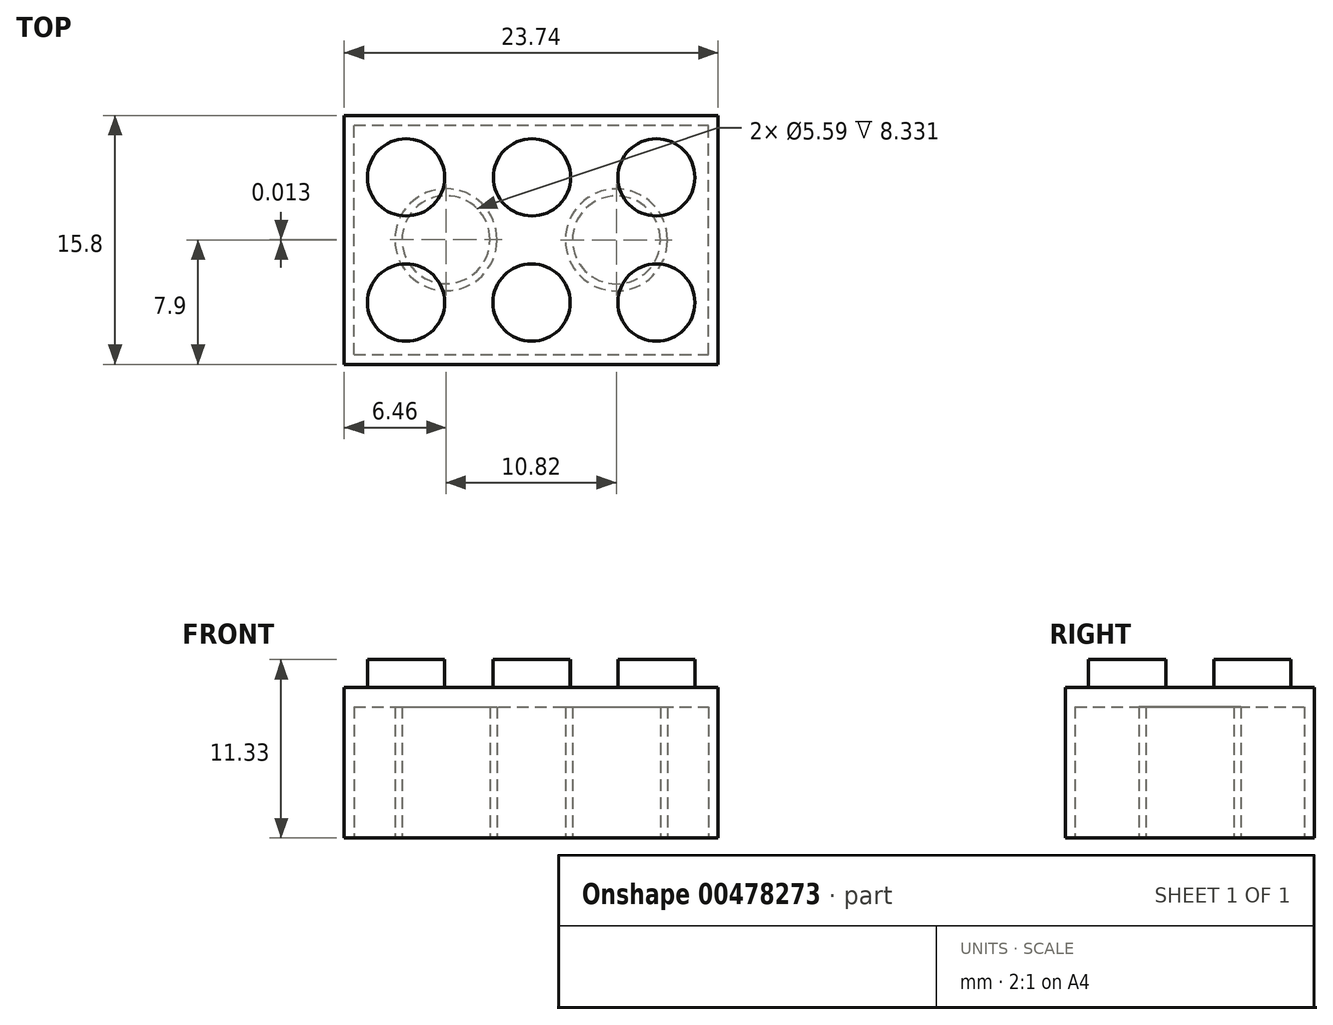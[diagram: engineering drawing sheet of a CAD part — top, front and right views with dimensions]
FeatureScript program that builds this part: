
annotation { "Feature Type Name" : "Feature", "Feature Type Description" : "" }
export const myFeature = defineFeature(function(context is Context, id is Id, definition is map)
    precondition{}
    {
        {
            var Q0;
            Q0=qCreatedBy(makeId("Top.planeOp"),FACE);
            var sketch = newSketch(context, id + "F0", { "sketchPlane" : qUnion([Q0])});
            skLineSegment(sketch, "E0.bottom", {"start": v(-11.87, 7.9) * mm, "end": v(11.87, 7.9) * mm});
            skLineSegment(sketch, "E0.top", {"start": v(-11.87, -7.9) * mm, "end": v(11.87, -7.9) * mm});
            skLineSegment(sketch, "E0.left", {"start": v(-11.87, 7.9) * mm, "end": v(-11.87, -7.9) * mm});
            skLineSegment(sketch, "E0.right", {"start": v(11.87, 7.9) * mm, "end": v(11.87, -7.9) * mm});
            skPoint(sketch, "E0.middle", {"position": v(0, 0) * mm});
            skSolve(sketch);
        }
        {
            var Q0;
            Q0=makeQuery(id+"F0.imprint","IMPRINT",FACE,{"disambiguationData":[TD([[makeQuery(id+"F0.imprint","IMPRINT",EDGE,{"derivedFrom":sQuery(id+"F0.wireOp",EDGE,"E0.bottom")}),-1.0]])]});
            extrude(context, id + "F1", {"entities" : qUnion([Q0]), "depth" : 9.55 * mm});
        }
        {
            var Q0;
            Q0=makeQuery(id+"F1.opExtrude","CAP_FACE",FACE,{"disambiguationData":[OSD([sQuery(id+"F0.wireOp",EDGE,"E0.bottom"),sQuery(id+"F0.wireOp",EDGE,"E0.top"),sQuery(id+"F0.wireOp",EDGE,"E0.left"),sQuery(id+"F0.wireOp",EDGE,"E0.right")])],"isStart":false});
            var sketch = newSketch(context, id + "F2", { "sketchPlane" : qUnion([Q0])});
            skCircle(sketch, "E1", {"center": v(-7.95, 3.98) * mm, "radius": 2.45 * mm});
            skSolve(sketch);
        }
        {
            var Q0;
            Q0=makeQuery(id+"F2.imprint","IMPRINT",FACE,{"disambiguationData":[TD([[makeQuery(id+"F2.imprint","IMPRINT",EDGE,{"derivedFrom":sQuery(id+"F2.wireOp",EDGE,"E1")}),-1.0]])]});
            var sketch = newSketch(context, id + "F3", { "sketchPlane" : qUnion([Q0])});
            skCircle(sketch, "E2", {"center": v(0.05, 3.98) * mm, "radius": 2.45 * mm});
            skSolve(sketch);
        }
        {
            var Q0;
            Q0=makeQuery(id+"F2.imprint","IMPRINT",FACE,{"disambiguationData":[TD([[makeQuery(id+"F2.imprint","IMPRINT",EDGE,{"derivedFrom":sQuery(id+"F2.wireOp",EDGE,"E1")}),-1.0]])]});
            var sketch = newSketch(context, id + "F4", { "sketchPlane" : qUnion([Q0])});
            skCircle(sketch, "E3", {"center": v(7.95, 3.98) * mm, "radius": 2.45 * mm});
            skSolve(sketch);
        }
        {
            var Q0;
            Q0=makeQuery(id+"F2.imprint","IMPRINT",FACE,{"disambiguationData":[TD([[makeQuery(id+"F2.imprint","IMPRINT",EDGE,{"derivedFrom":sQuery(id+"F2.wireOp",EDGE,"E1")}),-1.0]])]});
            var sketch = newSketch(context, id + "F5", { "sketchPlane" : qUnion([Q0])});
            skCircle(sketch, "E4", {"center": v(-7.95, -3.98) * mm, "radius": 2.45 * mm});
            skSolve(sketch);
        }
        {
            var Q0;
            Q0=makeQuery(id+"F2.imprint","IMPRINT",FACE,{"disambiguationData":[TD([[makeQuery(id+"F2.imprint","IMPRINT",EDGE,{"derivedFrom":sQuery(id+"F2.wireOp",EDGE,"E1")}),-1.0]])]});
            var sketch = newSketch(context, id + "F6", { "sketchPlane" : qUnion([Q0])});
            skCircle(sketch, "E5", {"center": v(7.95, -3.98) * mm, "radius": 2.45 * mm});
            skSolve(sketch);
        }
        {
            var Q0;
            Q0=makeQuery(id+"F2.imprint","IMPRINT",FACE,{"disambiguationData":[TD([[makeQuery(id+"F2.imprint","IMPRINT",EDGE,{"derivedFrom":sQuery(id+"F2.wireOp",EDGE,"E1")}),-1.0]])]});
            var sketch = newSketch(context, id + "F7", { "sketchPlane" : qUnion([Q0])});
            skCircle(sketch, "E6", {"center": v(0.03, -3.98) * mm, "radius": 2.45 * mm});
            skSolve(sketch);
        }
        {
            var Q0;
            Q0=makeQuery(id+"F2.imprint","IMPRINT",FACE,{"disambiguationData":[TD([[makeQuery(id+"F2.imprint","IMPRINT",EDGE,{"derivedFrom":sQuery(id+"F2.wireOp",EDGE,"E1")}),1.0]])]});
            extrude(context, id + "F8", {"entities" : qUnion([Q0]), "operationType" : NewBodyOperationType.ADD, "depth" : 1.78 * mm});
        }
        {
            var Q0;
            Q0=makeQuery(id+"F4.imprint","IMPRINT",FACE,{"disambiguationData":[TD([[makeQuery(id+"F4.imprint","IMPRINT",EDGE,{"derivedFrom":sQuery(id+"F4.wireOp",EDGE,"E3")}),1.0]])]});
            extrude(context, id + "F9", {"entities" : qUnion([Q0]), "operationType" : NewBodyOperationType.ADD, "depth" : 1.78 * mm});
        }
        {
            var Q0;
            Q0=makeQuery(id+"F6.imprint","IMPRINT",FACE,{"disambiguationData":[TD([[makeQuery(id+"F6.imprint","IMPRINT",EDGE,{"derivedFrom":sQuery(id+"F6.wireOp",EDGE,"E5")}),1.0]])]});
            extrude(context, id + "F10", {"entities" : qUnion([Q0]), "operationType" : NewBodyOperationType.ADD, "depth" : 1.78 * mm});
        }
        {
            var Q0;
            Q0=makeQuery(id+"F3.imprint","IMPRINT",FACE,{"disambiguationData":[TD([[makeQuery(id+"F3.imprint","IMPRINT",EDGE,{"derivedFrom":sQuery(id+"F3.wireOp",EDGE,"E2")}),1.0]])]});
            extrude(context, id + "F11", {"entities" : qUnion([Q0]), "operationType" : NewBodyOperationType.ADD, "depth" : 1.78 * mm});
        }
        {
            var Q0;
            Q0=makeQuery(id+"F5.imprint","IMPRINT",FACE,{"disambiguationData":[TD([[makeQuery(id+"F5.imprint","IMPRINT",EDGE,{"derivedFrom":sQuery(id+"F5.wireOp",EDGE,"E4")}),1.0]])]});
            extrude(context, id + "F12", {"entities" : qUnion([Q0]), "operationType" : NewBodyOperationType.ADD, "depth" : 1.78 * mm});
        }
        {
            var Q0;
            Q0=makeQuery(id+"F7.imprint","IMPRINT",FACE,{"disambiguationData":[TD([[makeQuery(id+"F7.imprint","IMPRINT",EDGE,{"derivedFrom":sQuery(id+"F7.wireOp",EDGE,"E6")}),1.0]])]});
            extrude(context, id + "F13", {"entities" : qUnion([Q0]), "operationType" : NewBodyOperationType.ADD, "depth" : 1.78 * mm});
        }
        {
            var Q0;
            Q0=makeQuery(id+"F1.opExtrude","CAP_FACE",FACE,{"disambiguationData":[OSD([sQuery(id+"F0.wireOp",EDGE,"E0.bottom"),sQuery(id+"F0.wireOp",EDGE,"E0.top"),sQuery(id+"F0.wireOp",EDGE,"E0.left"),sQuery(id+"F0.wireOp",EDGE,"E0.right")])],"isStart":true});
            var sketch = newSketch(context, id + "F14", { "sketchPlane" : qUnion([Q0])});
            skLineSegment(sketch, "E7.bottom", {"start": v(-11.26, 7.29) * mm, "end": v(11.26, 7.29) * mm});
            skLineSegment(sketch, "E7.top", {"start": v(-11.26, -7.29) * mm, "end": v(11.26, -7.29) * mm});
            skLineSegment(sketch, "E7.left", {"start": v(-11.26, 7.29) * mm, "end": v(-11.26, -7.29) * mm});
            skLineSegment(sketch, "E7.right", {"start": v(11.26, 7.29) * mm, "end": v(11.26, -7.29) * mm});
            skPoint(sketch, "E7.middle", {"position": v(0, 0) * mm});
            skSolve(sketch);
        }
        {
            var Q0;
            Q0=makeQuery(id+"F14.imprint","IMPRINT",FACE,{"disambiguationData":[TD([[makeQuery(id+"F14.imprint","IMPRINT",EDGE,{"derivedFrom":sQuery(id+"F14.wireOp",EDGE,"E7.bottom")}),-1.0]])]});
            var sketch = newSketch(context, id + "F15", { "sketchPlane" : qUnion([Q0])});
            skCircle(sketch, "E8", {"center": v(-5.41, -0.01) * mm, "radius": 3.24 * mm});
            skSolve(sketch);
        }
        {
            var Q0;
            Q0=makeQuery(id+"F14.imprint","IMPRINT",FACE,{"disambiguationData":[TD([[makeQuery(id+"F14.imprint","IMPRINT",EDGE,{"derivedFrom":sQuery(id+"F14.wireOp",EDGE,"E7.bottom")}),-1.0]])]});
            var sketch = newSketch(context, id + "F16", { "sketchPlane" : qUnion([Q0])});
            skCircle(sketch, "E9", {"center": v(5.41, 0) * mm, "radius": 3.24 * mm});
            skSolve(sketch);
        }
        {
            var Q0;
            Q0=makeQuery(id+"F14.imprint","IMPRINT",FACE,{"disambiguationData":[TD([[makeQuery(id+"F14.imprint","IMPRINT",EDGE,{"derivedFrom":sQuery(id+"F14.wireOp",EDGE,"E7.bottom")}),-1.0]])]});
            extrude(context, id + "F17", {"entities" : qUnion([Q0]), "operationType" : NewBodyOperationType.REMOVE, "oppositeDirection" : true, "depth" : 8.33 * mm, "offsetDistance" : 25.4 * mm});
        }
        {
            var Q0;
            Q0=makeQuery(id+"F15.imprint","IMPRINT",FACE,{"disambiguationData":[TD([[makeQuery(id+"F15.imprint","IMPRINT",EDGE,{"derivedFrom":sQuery(id+"F15.wireOp",EDGE,"E8")}),1.0]])]});
            var Q1;
            Q1=sQuery(id+"F15.wireOp",EDGE,"E8");
            extrude(context, id + "F18", {"entities" : qUnion([Q0]), "operationType" : NewBodyOperationType.ADD, "surfaceEntities" : qUnion([Q1]), "oppositeDirection" : true, "depth" : 8.33 * mm, "offsetDistance" : 25.4 * mm});
        }
        {
            var Q0;
            Q0=makeQuery(id+"F16.imprint","IMPRINT",FACE,{"disambiguationData":[TD([[makeQuery(id+"F16.imprint","IMPRINT",EDGE,{"derivedFrom":sQuery(id+"F16.wireOp",EDGE,"E9")}),1.0]])]});
            extrude(context, id + "F19", {"entities" : qUnion([Q0]), "operationType" : NewBodyOperationType.ADD, "oppositeDirection" : true, "depth" : 8.33 * mm, "offsetDistance" : 25.4 * mm});
        }
        {
            var Q0;
            Q0=makeQuery(id+"F18.opExtrude","CAP_FACE",FACE,{"disambiguationData":[OSD([sQuery(id+"F15.wireOp",EDGE,"E8")])],"isStart":true});
            var sketch = newSketch(context, id + "F20", { "sketchPlane" : qUnion([Q0])});
            skCircle(sketch, "E10", {"center": v(-5.41, -0.01) * mm, "radius": 2.8 * mm});
            skSolve(sketch);
        }
        {
            var Q0;
            Q0=makeQuery(id+"F19.opExtrude","CAP_FACE",FACE,{"disambiguationData":[OSD([sQuery(id+"F16.wireOp",EDGE,"E9")])],"isStart":true});
            var sketch = newSketch(context, id + "F21", { "sketchPlane" : qUnion([Q0])});
            skCircle(sketch, "E11", {"center": v(5.41, 0) * mm, "radius": 2.8 * mm});
            skSolve(sketch);
        }
        {
            var Q0;
            Q0=makeQuery(id+"F20.imprint","IMPRINT",FACE,{"disambiguationData":[TD([[makeQuery(id+"F20.imprint","IMPRINT",EDGE,{"derivedFrom":sQuery(id+"F20.wireOp",EDGE,"E10")}),1.0]])]});
            extrude(context, id + "F22", {"entities" : qUnion([Q0]), "operationType" : NewBodyOperationType.REMOVE, "oppositeDirection" : true, "depth" : 8.33 * mm, "offsetDistance" : 25.4 * mm});
        }
        {
            var Q0;
            Q0=makeQuery(id+"F21.imprint","IMPRINT",FACE,{"disambiguationData":[TD([[makeQuery(id+"F21.imprint","IMPRINT",EDGE,{"derivedFrom":sQuery(id+"F21.wireOp",EDGE,"E11")}),1.0]])]});
            extrude(context, id + "F23", {"entities" : qUnion([Q0]), "operationType" : NewBodyOperationType.REMOVE, "oppositeDirection" : true, "depth" : 8.33 * mm, "offsetDistance" : 25.4 * mm});
        }
    });
